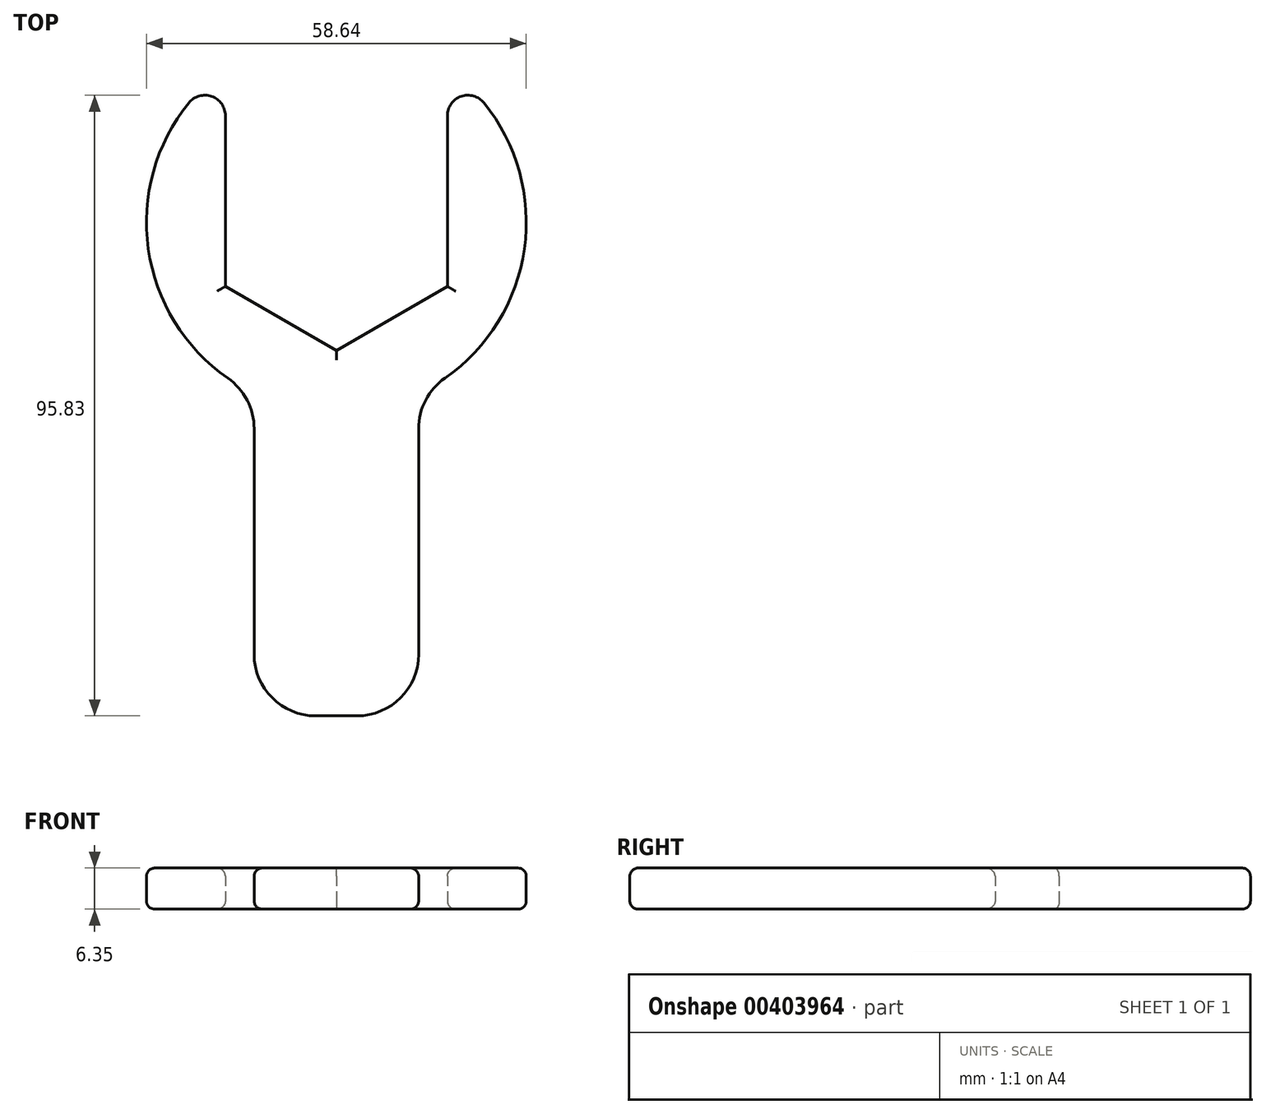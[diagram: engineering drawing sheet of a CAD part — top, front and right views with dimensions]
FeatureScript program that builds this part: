
annotation { "Feature Type Name" : "Feature", "Feature Type Description" : "" }
export const myFeature = defineFeature(function(context is Context, id is Id, definition is map)
    precondition{}
    {
        {
            var Q0;
            Q0=qCreatedBy(makeId("Top.planeOp"),FACE);
            var sketch = newSketch(context, id + "F0", { "sketchPlane" : qUnion([Q0])});
            skCircle(sketch, "E0.cCircle", {"center": v(0, 0) * mm, "radius": 17.15 * mm, "construction": true});
            skLineSegment(sketch, "E0.0", {"start": v(17.15, 9.9) * mm, "end": v(17.15, -9.9) * mm});
            skLineSegment(sketch, "E0.1", {"start": v(17.15, -9.9) * mm, "end": v(0, -19.8) * mm});
            skLineSegment(sketch, "E0.2", {"start": v(0, -19.8) * mm, "end": v(-17.15, -9.9) * mm});
            skLineSegment(sketch, "E0.3", {"start": v(-17.15, -9.9) * mm, "end": v(-17.15, 9.9) * mm});
            skLineSegment(sketch, "E0.4", {"start": v(-17.15, 9.9) * mm, "end": v(0, 19.8) * mm, "construction": true});
            skLineSegment(sketch, "E0.5", {"start": v(0, 19.8) * mm, "end": v(17.15, 9.9) * mm, "construction": true});
            skPoint(sketch, "E0.0.midPoint", {"position": v(17.15, 0) * mm});
            skArc(sketch, "E1", {"start": v(-22.79, 18.45) * mm, "mid": v(-29.03, -4.1) * mm, "end": v(-16.78, -24.05) * mm});
            skLineSegment(sketch, "E2", {"start": v(-17.15, 9.9) * mm, "end": v(-17.15, 16.46) * mm});
            skLineSegment(sketch, "E3", {"start": v(17.15, 16.46) * mm, "end": v(17.15, 9.9) * mm});
            skLineSegment(sketch, "E4", {"start": v(-12.7, -31.86) * mm, "end": v(-12.7, -66.67) * mm});
            skLineSegment(sketch, "E5", {"start": v(-3.17, -76.2) * mm, "end": v(3.18, -76.2) * mm});
            skLineSegment(sketch, "E6", {"start": v(12.7, -66.67) * mm, "end": v(12.7, -31.86) * mm});
            skArc(sketch, "E7.trimOffspring", {"start": v(16.78, -24.05) * mm, "mid": v(29.03, -4.1) * mm, "end": v(22.79, 18.45) * mm});
            skPoint(sketch, "E8.visualSharp", {"position": v(-12.7, -26.43) * mm});
            skArc(sketch, "E8.filletArc", {"start": v(-12.7, -31.86) * mm, "mid": v(-13.78, -27.46) * mm, "end": v(-16.78, -24.05) * mm});
            skPoint(sketch, "E9.visualSharp", {"position": v(12.7, -26.43) * mm});
            skArc(sketch, "E9.filletArc", {"start": v(16.78, -24.05) * mm, "mid": v(13.78, -27.46) * mm, "end": v(12.7, -31.86) * mm});
            skPoint(sketch, "E10.visualSharp", {"position": v(12.7, -76.2) * mm});
            skArc(sketch, "E10.filletArc", {"start": v(3.18, -76.2) * mm, "mid": v(9.91, -73.41) * mm, "end": v(12.7, -66.67) * mm});
            skPoint(sketch, "E11.visualSharp", {"position": v(-12.7, -76.2) * mm});
            skArc(sketch, "E11.filletArc", {"start": v(-12.7, -66.67) * mm, "mid": v(-9.91, -73.41) * mm, "end": v(-3.17, -76.2) * mm});
            skPoint(sketch, "E12.visualSharp", {"position": v(-17.15, 23.79) * mm});
            skArc(sketch, "E12.filletArc", {"start": v(-17.15, 16.46) * mm, "mid": v(-19.26, 19.45) * mm, "end": v(-22.79, 18.45) * mm});
            skPoint(sketch, "E13.visualSharp", {"position": v(17.15, 23.79) * mm});
            skArc(sketch, "E13.filletArc", {"start": v(22.79, 18.45) * mm, "mid": v(19.26, 19.45) * mm, "end": v(17.15, 16.46) * mm});
            skSolve(sketch);
        }
        {
            var Q0;
            Q0=makeQuery(id+"F0.imprint","IMPRINT",FACE,{"disambiguationData":[TD([[makeQuery(id+"F0.imprint","IMPRINT",EDGE,{"derivedFrom":sQuery(id+"F0.wireOp",EDGE,"E0.0")}),1.0]])]});
            extrude(context, id + "F1", {"entities" : qUnion([Q0]), "depth" : 6.35 * mm});
        }
        {
            var Q0;
            Q0=makeQuery(id+"F1.opExtrude","CAP_FACE",FACE,{"disambiguationData":[OSD([sQuery(id+"F0.wireOp",EDGE,"E0.0"),sQuery(id+"F0.wireOp",EDGE,"E0.1"),sQuery(id+"F0.wireOp",EDGE,"E0.2"),sQuery(id+"F0.wireOp",EDGE,"E0.3"),sQuery(id+"F0.wireOp",EDGE,"E1"),sQuery(id+"F0.wireOp",EDGE,"E2"),sQuery(id+"F0.wireOp",EDGE,"E3"),sQuery(id+"F0.wireOp",EDGE,"E4"),sQuery(id+"F0.wireOp",EDGE,"E5"),sQuery(id+"F0.wireOp",EDGE,"E6"),sQuery(id+"F0.wireOp",EDGE,"E7.trimOffspring"),sQuery(id+"F0.wireOp",EDGE,"E8.filletArc"),sQuery(id+"F0.wireOp",EDGE,"E9.filletArc"),sQuery(id+"F0.wireOp",EDGE,"E10.filletArc"),sQuery(id+"F0.wireOp",EDGE,"E11.filletArc"),sQuery(id+"F0.wireOp",EDGE,"E12.filletArc"),sQuery(id+"F0.wireOp",EDGE,"E13.filletArc")])],"isStart":false});
            var Q1;
            Q1=makeQuery(id+"F1.opExtrude","CAP_FACE",FACE,{"disambiguationData":[OSD([sQuery(id+"F0.wireOp",EDGE,"E0.0"),sQuery(id+"F0.wireOp",EDGE,"E0.1"),sQuery(id+"F0.wireOp",EDGE,"E0.2"),sQuery(id+"F0.wireOp",EDGE,"E0.3"),sQuery(id+"F0.wireOp",EDGE,"E1"),sQuery(id+"F0.wireOp",EDGE,"E2"),sQuery(id+"F0.wireOp",EDGE,"E3"),sQuery(id+"F0.wireOp",EDGE,"E4"),sQuery(id+"F0.wireOp",EDGE,"E5"),sQuery(id+"F0.wireOp",EDGE,"E6"),sQuery(id+"F0.wireOp",EDGE,"E7.trimOffspring"),sQuery(id+"F0.wireOp",EDGE,"E8.filletArc"),sQuery(id+"F0.wireOp",EDGE,"E9.filletArc"),sQuery(id+"F0.wireOp",EDGE,"E10.filletArc"),sQuery(id+"F0.wireOp",EDGE,"E11.filletArc"),sQuery(id+"F0.wireOp",EDGE,"E12.filletArc"),sQuery(id+"F0.wireOp",EDGE,"E13.filletArc")])],"isStart":true});
            fillet(context, id + "F2", {"entities" : qUnion([Q0, Q1]), "radius" : 1.27 * mm, "tangentPropagation" : true, "allowEdgeOverflow" : false});
        }
    });
